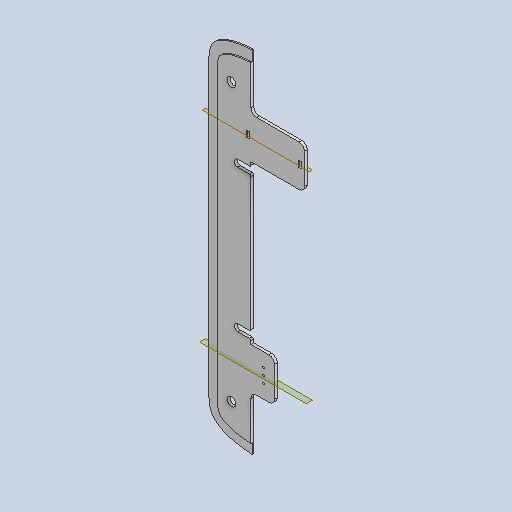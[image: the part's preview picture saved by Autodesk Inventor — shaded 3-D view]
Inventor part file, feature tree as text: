
AUTODESK INVENTOR PART (.ipt)
format: ipt  version: 2022 (Build 260153000, 153)  size: 424,448 bytes
history: native  units: mm
features: reference x22, other x10, extrude x5, sketch x5, fillet x3, projected_geometry x3
ambient origin geometry x8: Origin, YZ Plane, XZ Plane, XY Plane, X Axis, Y Axis, Z Axis, Center Point
bodies: Body1 (feature_tree)
feature tree (48):
  other  "Твердое тело1"
  extrude  "Выдавливание1"  Depth=3.3mm
  extrude  "Выдавливание2"  Depth=1.0mm TaperAngle=0.0deg
  fillet  "Сопряжение1"  Radius=0.5mm
  other  "РабПлоскость1"
  extrude  "Выдавливание3"  Depth=0.5mm
  extrude  "Выдавливание4"  Depth=2.0mm
  other  "РабПлоскость2"
  fillet  "Сопряжение2"  Radius=1.0mm
  fillet  "Сопряжение3"  Radius=3.0mm
  extrude  "Выдавливание5"  Depth=3.0mm
  sketch  "Эскиз1"
  reference  "Ссылка1"
  reference  "Ссылка2"
  reference  "Ссылка3"
  sketch  "Эскиз2"
  reference  "Ссылка4"
  reference  "Ссылка5"
  reference  "Ссылка6"
  projected_geometry  "Спроецированная петля1"
  reference  "Ссылка7"
  sketch  "Эскиз3"
  projected_geometry  "Спроецированная петля2"
  sketch  "Эскиз4"
  reference  "Ссылка8"
  projected_geometry  "Спроецированная петля3"
  reference  "Ссылка9"
  reference  "Ссылка10"
  reference  "Ссылка11"
  reference  "Ссылка12"
  reference  "Ссылка13"
  reference  "Ссылка14"
  reference  "Ссылка15"
  sketch  "Эскиз5"
  reference  "Ссылка16"
  reference  "Ссылка17"
  reference  "Ссылка18"
  reference  "Ссылка19"
  reference  "Ссылка20"
  reference  "Ссылка21"
  reference  "Ссылка22"
  other  "<userpath>\Documents\Git\MZCAT_2024_construction\MZCAT_2024\MZCAT_4.iam"
  other  "MZCAT_4.iam"
  other  "CAT_protector:1"
  other  "back_diffuser:1"
  other  "magazine_fixator:1"
  other  "vydacha_slide:1"
  other  "User Library-PLS-3:1"
